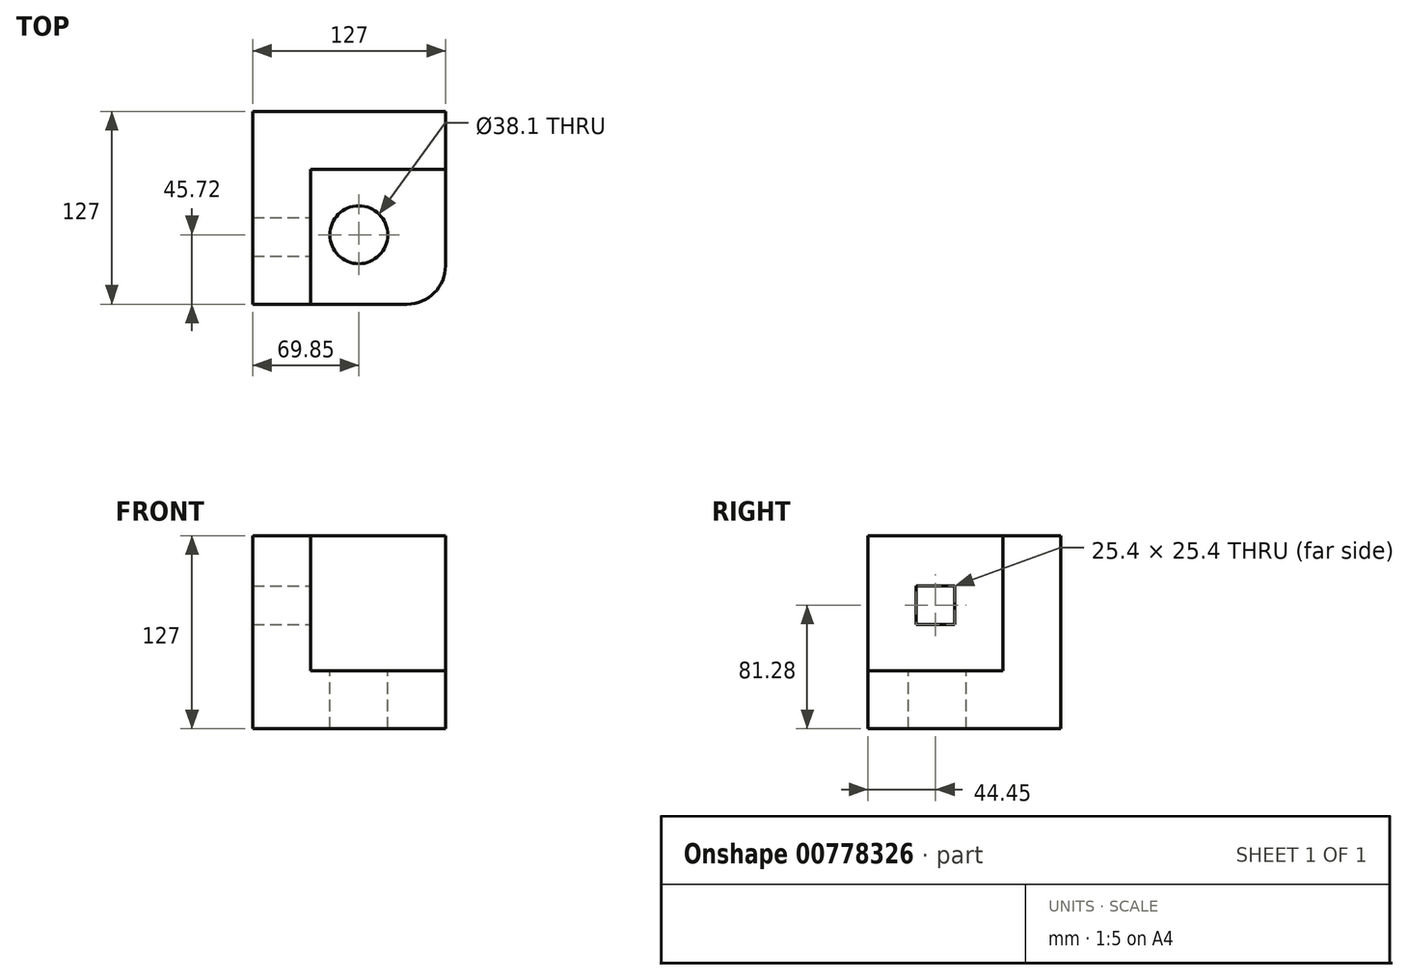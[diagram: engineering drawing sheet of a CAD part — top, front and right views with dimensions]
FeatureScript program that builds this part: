
annotation { "Feature Type Name" : "Feature", "Feature Type Description" : "" }
export const myFeature = defineFeature(function(context is Context, id is Id, definition is map)
    precondition{}
    {
        {
            var Q0;
            Q0=qCreatedBy(makeId("Front.planeOp"),FACE);
            var sketch = newSketch(context, id + "F0", { "sketchPlane" : qUnion([Q0])});
            skLineSegment(sketch, "E0.bottom", {"start": v(0, 0) * mm, "end": v(-127, 0) * mm});
            skLineSegment(sketch, "E0.top", {"start": v(0, 127) * mm, "end": v(-127, 127) * mm});
            skLineSegment(sketch, "E0.left", {"start": v(0, 0) * mm, "end": v(0, 127) * mm});
            skLineSegment(sketch, "E0.right", {"start": v(-127, 0) * mm, "end": v(-127, 127) * mm});
            skSolve(sketch);
        }
        {
            var Q0;
            Q0 = qSketchRegion(id + "F0", true);
            extrude(context, id + "F1", {"entities" : qUnion([Q0]), "depth" : 127 * mm, "offsetDistance" : 25.4 * mm});
        }
        {
            var Q0;
            Q0=makeQuery(id+"F1.opExtrude","CAP_FACE",FACE,{"disambiguationData":[OSD([sQuery(id+"F0.wireOp",EDGE,"E0.bottom"),sQuery(id+"F0.wireOp",EDGE,"E0.top"),sQuery(id+"F0.wireOp",EDGE,"E0.left"),sQuery(id+"F0.wireOp",EDGE,"E0.right")])],"isStart":false});
            var sketch = newSketch(context, id + "F2", { "sketchPlane" : qUnion([Q0])});
            skLineSegment(sketch, "E1", {"start": v(-127, 0) * mm, "end": v(-88.9, 0) * mm});
            skLineSegment(sketch, "E2", {"start": v(-88.9, 0) * mm, "end": v(-88.9, 38.1) * mm});
            skLineSegment(sketch, "E3", {"start": v(-88.9, 38.1) * mm, "end": v(-88.9, 127) * mm});
            skLineSegment(sketch, "E4", {"start": v(-88.9, 38.1) * mm, "end": v(0, 38.1) * mm});
            skLineSegment(sketch, "E5", {"start": v(0, 38.1) * mm, "end": v(0, 127) * mm});
            skLineSegment(sketch, "E6", {"start": v(0, 127) * mm, "end": v(-88.9, 127) * mm});
            skSolve(sketch);
        }
        {
            var Q0;
            Q0 = qSketchRegion(id + "F2", true);
            extrude(context, id + "F3", {"entities" : qUnion([Q0]), "operationType" : NewBodyOperationType.REMOVE, "oppositeDirection" : true, "depth" : 88.9 * mm, "offsetDistance" : 25.4 * mm});
        }
        {
            var Q0;
            Q0=makeQuery(id+"F1.opExtrude","CAP_EDGE",EDGE,{"disambiguationData":[OSD([sQuery(id+"F0.wireOp",EDGE,"E0.left")])],"isStart":false});
            fillet(context, id + "F4", {"entities" : qUnion([Q0]), "radius" : 25.4 * mm, "tangentPropagation" : true, "allowEdgeOverflow" : false});
        }
        {
            var Q0;
            Q0=makeQuery(id+"F3.boolean.opBoolean","COPY",FACE,{"derivedFrom":makeQuery(id+"F3.opExtrude","SWEPT_FACE",FACE,{"disambiguationData":[OSD([sQuery(id+"F2.wireOp",EDGE,"E3")])]})});
            var sketch = newSketch(context, id + "F5", { "sketchPlane" : qUnion([Q0])});
            skLineSegment(sketch, "E7", {"start": v(-127, 127) * mm, "end": v(-127, 93.98) * mm});
            skLineSegment(sketch, "E8", {"start": v(-127, 93.98) * mm, "end": v(-95.25, 93.98) * mm});
            skLineSegment(sketch, "E9", {"start": v(-95.25, 93.98) * mm, "end": v(-69.85, 93.98) * mm});
            skLineSegment(sketch, "E10", {"start": v(-69.85, 93.98) * mm, "end": v(-69.85, 68.58) * mm});
            skLineSegment(sketch, "E11", {"start": v(-69.85, 68.58) * mm, "end": v(-95.25, 68.58) * mm});
            skLineSegment(sketch, "E12", {"start": v(-95.25, 68.58) * mm, "end": v(-95.25, 93.98) * mm});
            skSolve(sketch);
        }
        {
            var Q0;
            Q0=makeQuery(id+"F5.imprint","IMPRINT",FACE,{"disambiguationData":[TD([[makeQuery(id+"F5.imprint","IMPRINT",EDGE,{"derivedFrom":sQuery(id+"F5.wireOp",EDGE,"E9")}),-1.0]])]});
            extrude(context, id + "F6", {"entities" : qUnion([Q0]), "operationType" : NewBodyOperationType.REMOVE, "oppositeDirection" : true, "depth" : 38.1 * mm, "offsetDistance" : 25.4 * mm});
        }
        {
            var Q0;
            Q0=makeQuery(id+"F3.boolean.opBoolean","COPY",FACE,{"derivedFrom":makeQuery(id+"F3.opExtrude","SWEPT_FACE",FACE,{"disambiguationData":[OSD([sQuery(id+"F2.wireOp",EDGE,"E4")])]})});
            var sketch = newSketch(context, id + "F7", { "sketchPlane" : qUnion([Q0])});
            skLineSegment(sketch, "E13", {"start": v(-57.15, -127) * mm, "end": v(-57.15, -81.28) * mm});
            skCircle(sketch, "E14", {"center": v(-57.15, -81.28) * mm, "radius": 19.05 * mm});
            skSolve(sketch);
        }
        {
            var Q0;
            Q0=makeQuery(id+"F7.imprint","IMPRINT",FACE,{"disambiguationData":[TD([[makeQuery(id+"F7.imprint","IMPRINT",EDGE,{"derivedFrom":sQuery(id+"F7.wireOp",EDGE,"E14")}),1.0]])]});
            extrude(context, id + "F8", {"entities" : qUnion([Q0]), "operationType" : NewBodyOperationType.REMOVE, "oppositeDirection" : true, "depth" : 38.1 * mm, "offsetDistance" : 25.4 * mm});
        }
    });
